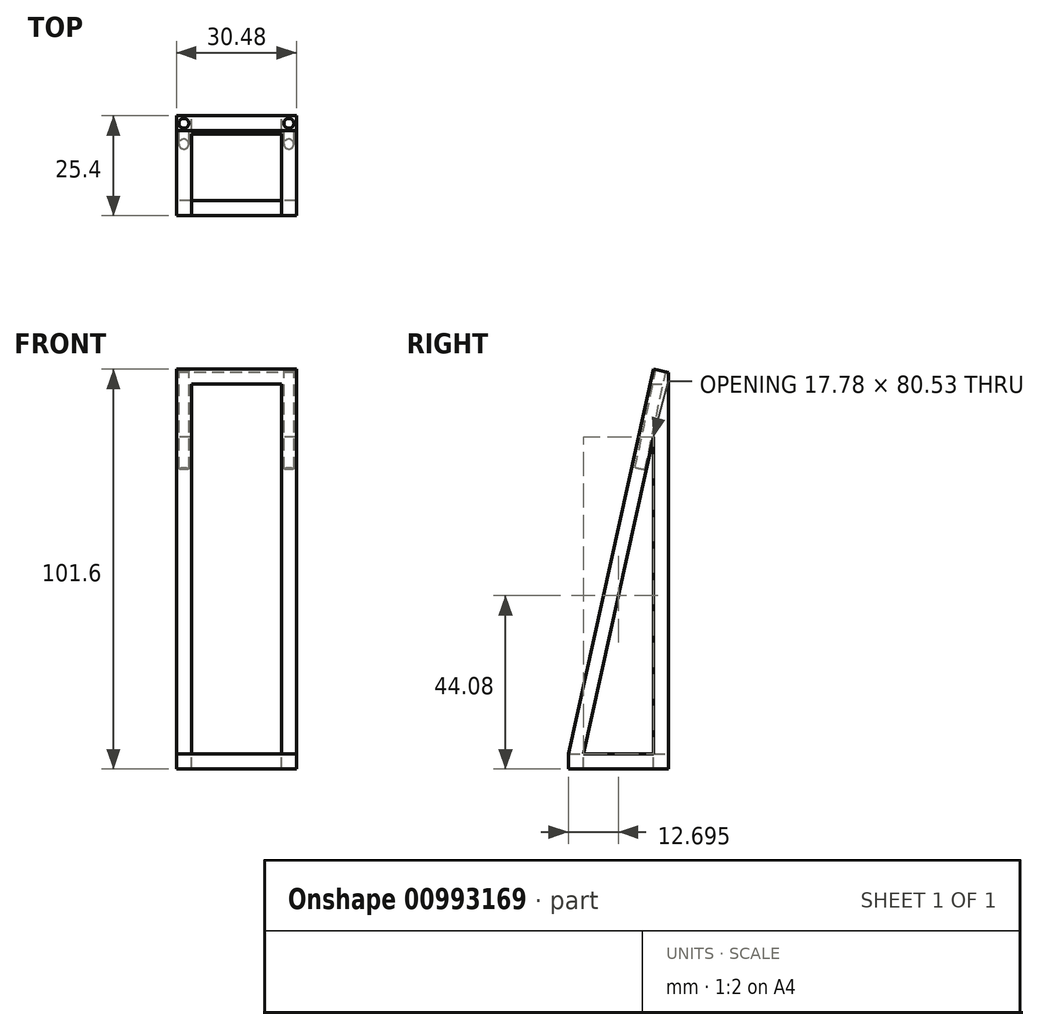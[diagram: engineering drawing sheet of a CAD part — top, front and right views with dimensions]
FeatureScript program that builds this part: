
annotation { "Feature Type Name" : "Feature", "Feature Type Description" : "" }
export const myFeature = defineFeature(function(context is Context, id is Id, definition is map)
    precondition{}
    {
        {
            var Q0;
            Q0=qCreatedBy(makeId("Right.planeOp"),FACE);
            var sketch = newSketch(context, id + "F0", { "sketchPlane" : qUnion([Q0])});
            skLineSegment(sketch, "E0.bottom", {"start": v(-52.35, -36.9) * mm, "end": v(-26.95, -36.9) * mm});
            skLineSegment(sketch, "E0.right", {"start": v(-26.95, -36.9) * mm, "end": v(-26.95, 64.7) * mm});
            skLineSegment(sketch, "E1", {"start": v(-30.76, 64.7) * mm, "end": v(-52.35, -33.1) * mm});
            skLineSegment(sketch, "E2", {"start": v(-52.35, -33.1) * mm, "end": v(-26.95, -33.1) * mm});
            skLineSegment(sketch, "E3", {"start": v(-26.95, 64.7) * mm, "end": v(-48.54, -33.1) * mm});
            skLineSegment(sketch, "E4", {"start": v(-30.76, 64.7) * mm, "end": v(-30.76, -33.1) * mm});
            skLineSegment(sketch, "E5", {"start": v(-30.76, 64.7) * mm, "end": v(-26.95, 64.7) * mm});
            skLineSegment(sketch, "E6", {"start": v(-52.35, -33.1) * mm, "end": v(-52.35, -36.9) * mm});
            skSolve(sketch);
        }
        {
            var Q0;
            {var subQ0=sQuery(id+"F0.wireOp",EDGE,"E1");Q0=makeQuery(id+"F0.imprint","IMPRINT",FACE,{"disambiguationData":[TD([[makeQuery(id+"F0.imprint","IMPRINT",EDGE,{"derivedFrom":subQ0}),1.0]])]});}
            var Q1;
            {var subQ4=sQuery(id+"F0.wireOp",EDGE,"E0.bottom");Q1=makeQuery(id+"F0.imprint","IMPRINT",FACE,{"disambiguationData":[TD([[makeQuery(id+"F0.imprint","IMPRINT",EDGE,{"derivedFrom":subQ4}),1.0]])]});}
            var Q2;
            {var subQ1=sQuery(id+"F0.wireOp",EDGE,"E0.right");var subQ3=sQuery(id+"F0.wireOp",EDGE,"E2");var subQ4=makeQuery(id+"F0.imprint","INTERSECT",VERTEX,{"derivedFrom":[subQ1,subQ3]});Q2=makeQuery(id+"F0.imprint","IMPRINT",FACE,{"disambiguationData":[TD([[makeQuery(id+"F0.imprint","IMPRINT",EDGE,{"disambiguationData":[TD([[subQ4,1.0]])],"derivedFrom":subQ3}),1.0]])]});}
            var Q3;
            {var subQ0=sQuery(id+"F0.wireOp",EDGE,"E5");Q3=makeQuery(id+"F0.imprint","IMPRINT",FACE,{"disambiguationData":[TD([[makeQuery(id+"F0.imprint","IMPRINT",EDGE,{"derivedFrom":subQ0}),-1.0]])]});}
            extrude(context, id + "F1", {"entities" : qUnion([Q0, Q1, Q2, Q3]), "depth" : 30.48 * mm, "offsetDistance" : 25.4 * mm});
        }
        {
            var Q0;
            Q0=makeQuery(id+"F1.opExtrude","SWEPT_FACE",FACE,{"disambiguationData":[OSD([sQuery(id+"F0.wireOp",EDGE,"E0.right")])]});
            var sketch = newSketch(context, id + "F2", { "sketchPlane" : qUnion([Q0])});
            skLineSegment(sketch, "E7.bottom", {"start": v(-26.67, 60.88) * mm, "end": v(-3.8, 60.88) * mm});
            skLineSegment(sketch, "E7.top", {"start": v(-26.67, -33.1) * mm, "end": v(-3.8, -33.1) * mm});
            skLineSegment(sketch, "E7.left", {"start": v(-26.67, 60.88) * mm, "end": v(-26.67, -33.1) * mm});
            skLineSegment(sketch, "E7.right", {"start": v(-3.8, 60.88) * mm, "end": v(-3.8, -33.1) * mm});
            skSolve(sketch);
        }
        {
            var Q0;
            Q0=makeQuery(id+"F2.imprint","IMPRINT",FACE,{"disambiguationData":[TD([[makeQuery(id+"F2.imprint","IMPRINT",EDGE,{"derivedFrom":sQuery(id+"F2.wireOp",EDGE,"E7.bottom")}),-1.0]])]});
            extrude(context, id + "F3", {"entities" : qUnion([Q0]), "operationType" : NewBodyOperationType.REMOVE, "oppositeDirection" : true, "depth" : 25.4 * mm, "offsetDistance" : 25.4 * mm});
        }
        {
            var Q0;
            Q0=makeQuery(id+"F3.boolean.opBoolean","MERGE",FACE,{"derivedFrom":[makeQuery(id+"F1.opExtrude","SWEPT_FACE",FACE,{"disambiguationData":[OSD([sQuery(id+"F0.wireOp",EDGE,"E2")])]})],"fromTools":[makeQuery(id+"F3.opExtrude","SWEPT_FACE",FACE,{"disambiguationData":[OSD([sQuery(id+"F2.wireOp",EDGE,"E7.top")])]})]});
            var sketch = newSketch(context, id + "F4", { "sketchPlane" : qUnion([Q0])});
            skLineSegment(sketch, "E8.bottom", {"start": v(26.67, -30.76) * mm, "end": v(3.8, -30.76) * mm});
            skLineSegment(sketch, "E8.top", {"start": v(26.67, -48.54) * mm, "end": v(3.8, -48.54) * mm});
            skLineSegment(sketch, "E8.left", {"start": v(26.67, -30.76) * mm, "end": v(26.67, -48.54) * mm});
            skLineSegment(sketch, "E8.right", {"start": v(3.8, -30.76) * mm, "end": v(3.8, -48.54) * mm});
            skSolve(sketch);
        }
        {
            var Q0;
            Q0=makeQuery(id+"F4.imprint","IMPRINT",FACE,{"disambiguationData":[TD([[makeQuery(id+"F4.imprint","IMPRINT",EDGE,{"derivedFrom":sQuery(id+"F4.wireOp",EDGE,"E8.bottom")}),1.0]])]});
            extrude(context, id + "F5", {"entities" : qUnion([Q0]), "operationType" : NewBodyOperationType.REMOVE, "oppositeDirection" : true, "depth" : 25.4 * mm, "offsetDistance" : 25.4 * mm});
        }
        {
            var Q0;
            Q0=makeQuery(id+"F1.opExtrude","CAP_FACE",FACE,{"disambiguationData":[OSD([sQuery(id+"F0.wireOp",EDGE,"E0.bottom"),sQuery(id+"F0.wireOp",EDGE,"E0.right"),sQuery(id+"F0.wireOp",EDGE,"E1"),sQuery(id+"F0.wireOp",EDGE,"E2"),sQuery(id+"F0.wireOp",EDGE,"E3"),sQuery(id+"F0.wireOp",EDGE,"E4"),sQuery(id+"F0.wireOp",EDGE,"E5"),sQuery(id+"F0.wireOp",EDGE,"E6")])],"isStart":true});
            var sketch = newSketch(context, id + "F6", { "sketchPlane" : qUnion([Q0])});
            skLineSegment(sketch, "E9", {"start": v(30.76, 64.7) * mm, "end": v(26.95, 63.88) * mm});
            skSolve(sketch);
        }
        {
            var Q0;
            {var subQ0=sQuery(id+"F6.wireOp",EDGE,"E9");Q0=makeQuery(id+"F6.imprint","IMPRINT",FACE,{"disambiguationData":[TD([[makeQuery(id+"F6.imprint","IMPRINT",EDGE,{"derivedFrom":subQ0}),-1.0]])]});}
            extrude(context, id + "F7", {"entities" : qUnion([Q0]), "operationType" : NewBodyOperationType.REMOVE, "oppositeDirection" : true, "depth" : 50.8 * mm, "offsetDistance" : 25.4 * mm});
        }
        {
            var Q0;
            Q0=makeQuery(id+"F7.boolean.opBoolean","COPY",FACE,{"derivedFrom":makeQuery(id+"F7.opExtrude","SWEPT_FACE",FACE,{"disambiguationData":[OSD([sQuery(id+"F6.wireOp",EDGE,"E9")])]})});
            var sketch = newSketch(context, id + "F8", { "sketchPlane" : qUnion([Q0])});
            skCircle(sketch, "E10", {"center": v(28.57, -41.6) * mm, "radius": 1.27 * mm});
            skPoint(sketch, "E10.centerSnap0", {"position": v(30.48, -41.6) * mm});
            skCircle(sketch, "E11", {"center": v(1.9, -41.6) * mm, "radius": 1.27 * mm});
            skPoint(sketch, "E11.centerSnap0", {"position": v(0, -41.6) * mm});
            skSolve(sketch);
        }
        {
            var Q0;
            Q0=makeQuery(id+"F8.imprint","IMPRINT",FACE,{"disambiguationData":[TD([[makeQuery(id+"F8.imprint","IMPRINT",EDGE,{"derivedFrom":sQuery(id+"F8.wireOp",EDGE,"E10")}),1.0]])]});
            var Q1;
            Q1=makeQuery(id+"F8.imprint","IMPRINT",FACE,{"disambiguationData":[TD([[makeQuery(id+"F8.imprint","IMPRINT",EDGE,{"derivedFrom":sQuery(id+"F8.wireOp",EDGE,"E11")}),1.0]])]});
            extrude(context, id + "F9", {"entities" : qUnion([Q0, Q1]), "operationType" : NewBodyOperationType.REMOVE, "oppositeDirection" : true, "depth" : 25.4 * mm, "offsetDistance" : 25.4 * mm});
        }
    });
